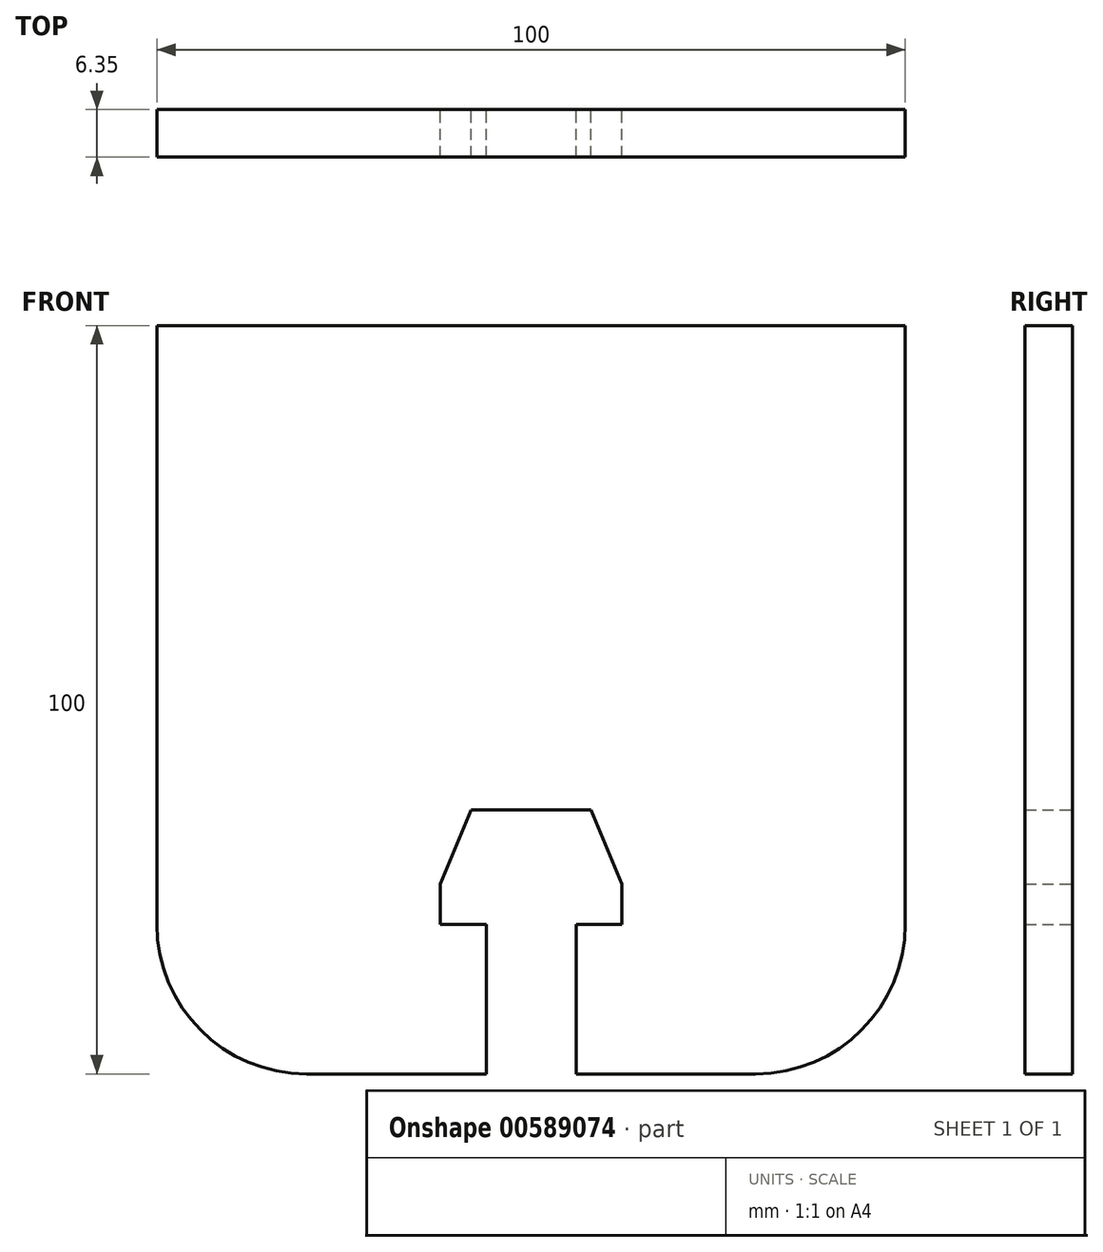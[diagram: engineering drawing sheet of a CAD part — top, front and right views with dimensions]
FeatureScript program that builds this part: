
annotation { "Feature Type Name" : "Feature", "Feature Type Description" : "" }
export const myFeature = defineFeature(function(context is Context, id is Id, definition is map)
    precondition{}
    {
        {
            var Q0;
            Q0=qCreatedBy(makeId("Front.planeOp"),FACE);
            var sketch = newSketch(context, id + "F0", { "sketchPlane" : qUnion([Q0])});
            skLineSegment(sketch, "E0.bottom", {"start": v(-50, 50) * mm, "end": v(50, 50) * mm});
            skLineSegment(sketch, "E0.top", {"start": v(-30, -50) * mm, "end": v(-6, -50) * mm});
            skLineSegment(sketch, "E0.left", {"start": v(-50, 50) * mm, "end": v(-50, -30) * mm});
            skLineSegment(sketch, "E0.right", {"start": v(50, 50) * mm, "end": v(50, -30) * mm});
            skLineSegment(sketch, "E1", {"start": v(-50, 0) * mm, "end": v(50, 0) * mm, "construction": true});
            skLineSegment(sketch, "E2", {"start": v(0, 50) * mm, "end": v(0, -50) * mm, "construction": true});
            skPoint(sketch, "E3.visualSharp", {"position": v(-50, -50) * mm});
            skArc(sketch, "E3.filletArc", {"start": v(-50, -30) * mm, "mid": v(-44.14, -44.14) * mm, "end": v(-30, -50) * mm});
            skPoint(sketch, "E4.visualSharp", {"position": v(50, -50) * mm});
            skArc(sketch, "E4.filletArc", {"start": v(30, -50) * mm, "mid": v(44.14, -44.14) * mm, "end": v(50, -30) * mm});
            skLineSegment(sketch, "E5", {"start": v(-8, -14.7) * mm, "end": v(8, -14.7) * mm});
            skLineSegment(sketch, "E6", {"start": v(8, -14.7) * mm, "end": v(12.15, -24.6) * mm});
            skLineSegment(sketch, "E7", {"start": v(12.15, -24.6) * mm, "end": v(12.15, -30) * mm});
            skLineSegment(sketch, "E8", {"start": v(12.15, -30) * mm, "end": v(6, -30) * mm});
            skLineSegment(sketch, "E9", {"start": v(-12.15, -30) * mm, "end": v(-12.15, -24.6) * mm});
            skLineSegment(sketch, "E10", {"start": v(-12.15, -24.6) * mm, "end": v(-8, -14.7) * mm});
            skPoint(sketch, "E11", {"position": v(0, -14.7) * mm});
            skPoint(sketch, "E12", {"position": v(0, -30) * mm});
            skLineSegment(sketch, "E13", {"start": v(6, -30) * mm, "end": v(6, -50) * mm});
            skLineSegment(sketch, "E14.MirrorCS", {"start": v(-6, -30) * mm, "end": v(-6, -50) * mm});
            skLineSegment(sketch, "E15.trimOffspring", {"start": v(-6, -30) * mm, "end": v(-12.15, -30) * mm});
            skLineSegment(sketch, "E16.trimOffspring", {"start": v(6, -50) * mm, "end": v(30, -50) * mm});
            skSolve(sketch);
        }
        {
            var Q0;
            Q0 = qSketchRegion(id + "F0", true);
            extrude(context, id + "F1", {"entities" : qUnion([Q0]), "depth" : 6.35 * mm, "offsetDistance" : 25 * mm});
        }
    });
